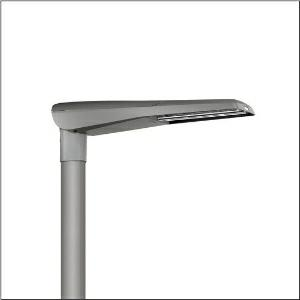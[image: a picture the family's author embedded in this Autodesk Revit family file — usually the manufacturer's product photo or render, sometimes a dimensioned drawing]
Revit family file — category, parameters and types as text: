
# Revit family: streetlight_sl_11_iq_mini___st1_2a_5xc2ac1f08ge_c732
name_source: partatom
category: Lighting Fixtures
units: mm (PartAtom-declared; Revit-internal decimal feet)

## family parameters
Cut with Voids When Loaded = No
Host = Face
Light Source = No
Part Type = Normal
Room Calculation Point = No
Round Connector Dimension = Use Diameter
Shared = No

## types (1)
- --- (1 x LED, 3040 lm, 25.3 W, 2200K)
    Apparent Load = 25 VA
    CIE Flux Codes = 32 70 96 100 100
    Color Rendering = 70
    Color Temperature = 2200K
    Default Elevation = 1800 mm
    Description = Streetlight SL 11 iQ mini, mast luminaire, primary light control with 3 zone facetted reflector, of plastic, silver coated, highly specular, primary optical cover: cover, of PMMA, transparent, light distribution: ST1.2a, light emission: direct distribution, primary light characteristic: asymmetric, installation type: post-top, side-entry, lamps: LED, High Power LED, rated values: 3.570lm | 24,9W | 143,4lm/W (begin service life); end service life: 3.570lm | 25,7W; at 50% lumin. flux: 1.785lm | 12,8W | 139,5lm/W, colour temperature: 2200/2700/3000/4000K, colour rendering: CRI > 70, light colour: 722/727/730/740, light setting 1 begin service life: 100% | 3.570lm | 24,9W | 143,4lm/W | 3.000K, light setting 1 end service life: 25,7W, further light settings possible, control: Street-Remote, Auto-Match, Temp-Guard, Lumen-Switch, Night-Set, Smart-Wire, Light-Fading, Desk-Remote (wireless, voltage-free reading and setting of iQ features in the workshop via application-optimized NFC function/RFID function), optimised constant luminous flux control (CLO 2.0), with cable H07RN-F 5x 1.5mm², mains connection: 230..240V, AC, 50/60Hz, connection cable pre-assembled, cable length: 6,5m, luminaire housing, of diecast aluminium, powder-coated, Siteco® metallic grey (DB 702S), please order mast flange separately, inclination adjustable without tools: 0°, 5°, 10°, 15° (post-top) | 0°, -5°, -10°, -15° (side-entry), sealing non-destructively replaceable, multi-level sealing system, length: 736mm, width: 174mm, height: 116mm, mast flange for spigot size: 42mm (side-entry): 5XC10008XM4, 60/48mm (side-entry/post-top): 5XC10108XM2, 76/60mm (side-entry/post-top): 5XC10108XM1, equipment: standard, protection rating (complete): IP66, insulation class (complete): insulation class II (safety insulation), certification: CE, ENEC, ENEC+, VDE, impact resistance: IK10, permissible operating ambient temperature for outdoor applications: -25..+50°C, standard-compliant lighting for roads and squares, Environmental Product Declaration (EPD) tested and certified by an independent institute, packaging unit: 1 piece

Light Distribution: ST1.2a
    Height = 116 mm
    Lamp = 1 x LED
    Lamp Light Flux = 3040 lm
    Lamp Power = 25.3 W
    Lamp count = 1
    Length = 736 mm
    Luminous efficacy = 120 lm/W
    Manufacturer = Siteco
    ModVariant = No
    Model = 5XC2AC1F08GE
    Number of Poles = 1
    OnlyDefault = Yes
    Power Factor = 1
    Product Name = Streetlight SL 11 iQ mini | ST1.2a
    Product group = mast luminaire | pylon top
    ProductGroupID = 6100
    Protection Class = Protection class II
    Protection Degree = IP 66
    RLX_Detail_Level = 1
    RLX_Emergency_Light_Flux = 0 lm
    RLX_Emergency_Type = 0
    RLX_Emergency_Type_DB = No
    RlxData = <blob elided: 53545 chars, md5=168e9ee0>
    Socket = socket
    Standby Power = 0 W
    System Light Flux = 3040 lm
    System Power = 25 W
    Type Comments = individual setting: luminous flux: 100 % | dim-lin: 254 | 351 mA
    Type Image = l_1003508.jpg
    URL = http://relux.com
    VarID = @adj_055553
    Voltage = 0 V
    Weight = 0.00 kg
    Width = 174 mm

## geometry (parser evidence)
native form markers: Blend x4, Sweep x9
no freeform markers — native parametric forms only
